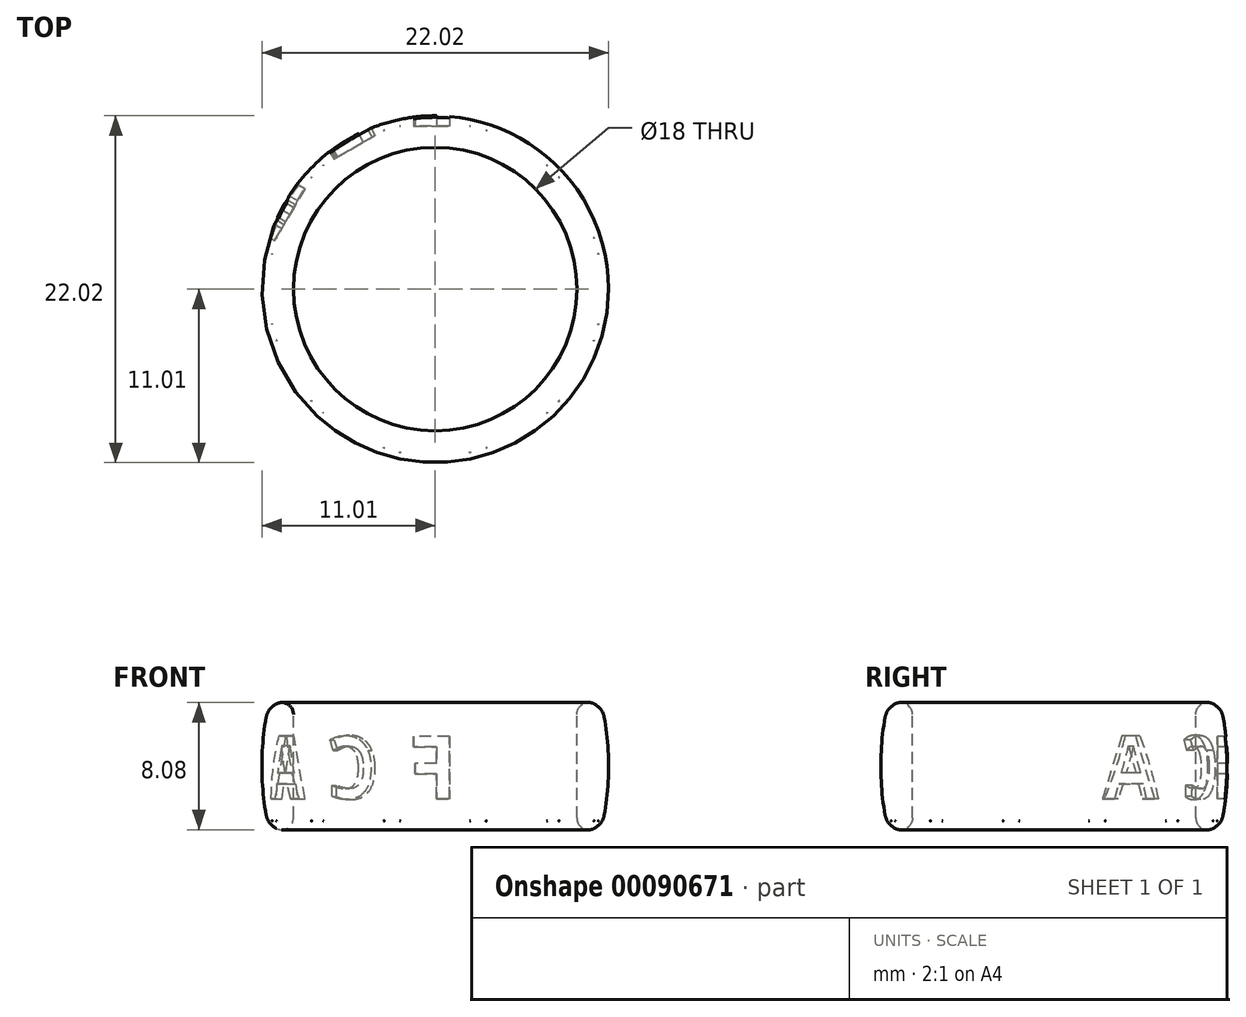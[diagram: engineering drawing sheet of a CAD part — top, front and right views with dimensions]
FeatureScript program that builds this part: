
annotation { "Feature Type Name" : "Feature", "Feature Type Description" : "" }
export const myFeature = defineFeature(function(context is Context, id is Id, definition is map)
    precondition{}
    {
        {
            var Q0;
            Q0=qCreatedBy(makeId("Top.planeOp"),FACE);
            var sketch = newSketch(context, id + "F0", { "sketchPlane" : qUnion([Q0])});
            skCircle(sketch, "E0", {"center": v(0, 0) * mm, "radius": 9 * mm});
            skSolve(sketch);
        }
        {
            var Q0;
            Q0 = qSketchRegion(id + "F0", true);
            extrude(context, id + "F1", {"entities" : qUnion([Q0]), "depth" : 5 * mm});
        }
        {
            var Q0;
            Q0=qCreatedBy(makeId("Front.planeOp"),FACE);
            var sketch = newSketch(context, id + "F2", { "sketchPlane" : qUnion([Q0])});
            skLineSegment(sketch, "E1", {"start": v(-9, 0) * mm, "end": v(-9, 8.18) * mm});
            skLineSegment(sketch, "E2", {"start": v(-9, 8.18) * mm, "end": v(-10.5, 8.18) * mm});
            skLineSegment(sketch, "E3", {"start": v(-9, 0) * mm, "end": v(-10.5, 0) * mm});
            skEllipticalArc(sketch, "E4", {});
            const initialGuessF2  = {"E4": [-0.009, 0.004088467297574947, 0, 1, 0.006151676925641073, 0.0020075208455440164, 0.8438243033653899, 2.2977683502244024]};
            skSetInitialGuess(sketch, initialGuessF2);
            skSolve(sketch);
        }
        {
            var Q0;
            Q0=makeQuery(id+"F2.imprint","IMPRINT",FACE,{"disambiguationData":[TD([[makeQuery(id+"F2.imprint","IMPRINT",EDGE,{"derivedFrom":sQuery(id+"F2.wireOp",EDGE,"E1")}),1.0]])]});
            var Q1;
            Q1=makeQuery(id+"F1.opExtrude","SWEPT_FACE",FACE,{"disambiguationData":[OSD([sQuery(id+"F0.wireOp",EDGE,"E0")])]});
            revolve(context, id + "F3", {"entities" : qUnion([Q0]), "axis" : qUnion([Q1]), "revolveType" : RevolveType.FULL});
        }
        {
            var Q0;
            Q0=makeQuery(id+"F3.opRevolve","SWEPT_EDGE",EDGE,{"disambiguationData":[OSD([sQuery(id+"F2.wireOp",EDGE,"E2"),sQuery(id+"F2.wireOp",EDGE,"E4")])]});
            var Q1;
            Q1=makeQuery(id+"F3.opRevolve","SWEPT_EDGE",EDGE,{"disambiguationData":[OSD([sQuery(id+"F2.wireOp",EDGE,"E3"),sQuery(id+"F2.wireOp",EDGE,"E4")])]});
            fillet(context, id + "F4", {"entities" : qUnion([Q0, Q1]), "radius" : 1.2 * mm, "tangentPropagation" : true, "allowEdgeOverflow" : false});
        }
        {
            var Q0;
            Q0=makeQuery(id+"F3.opRevolve","SWEPT_EDGE",EDGE,{"disambiguationData":[OSD([sQuery(id+"F2.wireOp",EDGE,"E1"),sQuery(id+"F2.wireOp",EDGE,"E3")])]});
            var Q1;
            Q1=makeQuery(id+"F3.opRevolve","SWEPT_EDGE",EDGE,{"disambiguationData":[OSD([sQuery(id+"F2.wireOp",EDGE,"E1"),sQuery(id+"F2.wireOp",EDGE,"E2")])]});
            fillet(context, id + "F5", {"entities" : qUnion([Q0, Q1]), "radius" : .75 * mm, "tangentPropagation" : true, "allowEdgeOverflow" : false});
        }
        {
            var Q0;
            Q0=makeQuery(id+"F1.opExtrude","SWEPT_BODY",BODY,{"disambiguationData":[OSD([sQuery(id+"F0.wireOp",EDGE,"E0")])]});
            deleteBodies(context, id + "F6", {"entities" : qUnion([Q0])});
        }
        {
            var Q0;
            Q0=qCreatedBy(makeId("Top.planeOp"),FACE);
            cPlane(context, id + "F7", {"entities" : qUnion([Q0]), "cplaneType" : CPlaneType.OFFSET, "offset" : 7 * mm, "width" : 150 * mm, "height" : 150 * mm});
        }
        {
            var Q0;
            Q0=qCreatedBy(id+"F7.planeOp",FACE);
            var sketch = newSketch(context, id + "F8", { "sketchPlane" : qUnion([Q0])});
            skLineSegment(sketch, "E5.bottom", {"start": v(-2.25, -9.36) * mm, "end": v(2.25, -9.36) * mm});
            skLineSegment(sketch, "E5.top", {"start": v(-2.25, -10.36) * mm, "end": v(2.25, -10.36) * mm});
            skLineSegment(sketch, "E5.left", {"start": v(-2.25, -9.36) * mm, "end": v(-2.25, -10.36) * mm});
            skLineSegment(sketch, "E5.right", {"start": v(2.25, -9.36) * mm, "end": v(2.25, -10.36) * mm});
            skLineSegment(sketch, "E6.1.0", {"start": v(2.73, -9.23) * mm, "end": v(6.63, -6.98) * mm});
            skLineSegment(sketch, "E6.1.1", {"start": v(6.63, -6.98) * mm, "end": v(7.13, -7.85) * mm});
            skLineSegment(sketch, "E6.1.2", {"start": v(3.23, -10.1) * mm, "end": v(7.13, -7.85) * mm});
            skLineSegment(sketch, "E6.1.3", {"start": v(2.73, -9.23) * mm, "end": v(3.23, -10.1) * mm});
            skLineSegment(sketch, "E6.2.0", {"start": v(6.98, -6.63) * mm, "end": v(9.23, -2.73) * mm});
            skLineSegment(sketch, "E6.2.1", {"start": v(9.23, -2.73) * mm, "end": v(10.1, -3.23) * mm});
            skLineSegment(sketch, "E6.2.2", {"start": v(7.85, -7.13) * mm, "end": v(10.1, -3.23) * mm});
            skLineSegment(sketch, "E6.2.3", {"start": v(6.98, -6.63) * mm, "end": v(7.85, -7.13) * mm});
            skLineSegment(sketch, "E6.3.0", {"start": v(9.36, -2.25) * mm, "end": v(9.36, 2.25) * mm});
            skLineSegment(sketch, "E6.3.1", {"start": v(9.36, 2.25) * mm, "end": v(10.36, 2.25) * mm});
            skLineSegment(sketch, "E6.3.2", {"start": v(10.36, -2.25) * mm, "end": v(10.36, 2.25) * mm});
            skLineSegment(sketch, "E6.3.3", {"start": v(9.36, -2.25) * mm, "end": v(10.36, -2.25) * mm});
            skLineSegment(sketch, "E6.4.0", {"start": v(9.23, 2.73) * mm, "end": v(6.98, 6.63) * mm});
            skLineSegment(sketch, "E6.4.1", {"start": v(6.98, 6.63) * mm, "end": v(7.85, 7.13) * mm});
            skLineSegment(sketch, "E6.4.2", {"start": v(10.1, 3.23) * mm, "end": v(7.85, 7.13) * mm});
            skLineSegment(sketch, "E6.4.3", {"start": v(9.23, 2.73) * mm, "end": v(10.1, 3.23) * mm});
            skLineSegment(sketch, "E6.5.0", {"start": v(6.63, 6.98) * mm, "end": v(2.73, 9.23) * mm});
            skLineSegment(sketch, "E6.5.1", {"start": v(2.73, 9.23) * mm, "end": v(3.23, 10.1) * mm});
            skLineSegment(sketch, "E6.5.2", {"start": v(7.13, 7.85) * mm, "end": v(3.23, 10.1) * mm});
            skLineSegment(sketch, "E6.5.3", {"start": v(6.63, 6.98) * mm, "end": v(7.13, 7.85) * mm});
            skLineSegment(sketch, "E6.6.0", {"start": v(2.25, 9.36) * mm, "end": v(-2.25, 9.36) * mm});
            skLineSegment(sketch, "E6.6.1", {"start": v(-2.25, 9.36) * mm, "end": v(-2.25, 10.36) * mm});
            skLineSegment(sketch, "E6.6.2", {"start": v(2.25, 10.36) * mm, "end": v(-2.25, 10.36) * mm});
            skLineSegment(sketch, "E6.6.3", {"start": v(2.25, 9.36) * mm, "end": v(2.25, 10.36) * mm});
            skLineSegment(sketch, "E6.7.0", {"start": v(-2.73, 9.23) * mm, "end": v(-6.63, 6.98) * mm});
            skLineSegment(sketch, "E6.7.1", {"start": v(-6.63, 6.98) * mm, "end": v(-7.13, 7.85) * mm});
            skLineSegment(sketch, "E6.7.2", {"start": v(-3.23, 10.1) * mm, "end": v(-7.13, 7.85) * mm});
            skLineSegment(sketch, "E6.7.3", {"start": v(-2.73, 9.23) * mm, "end": v(-3.23, 10.1) * mm});
            skLineSegment(sketch, "E6.8.0", {"start": v(-6.98, 6.63) * mm, "end": v(-9.23, 2.73) * mm});
            skLineSegment(sketch, "E6.8.1", {"start": v(-9.23, 2.73) * mm, "end": v(-10.1, 3.23) * mm});
            skLineSegment(sketch, "E6.8.2", {"start": v(-7.85, 7.13) * mm, "end": v(-10.1, 3.23) * mm});
            skLineSegment(sketch, "E6.8.3", {"start": v(-6.98, 6.63) * mm, "end": v(-7.85, 7.13) * mm});
            skLineSegment(sketch, "E6.9.0", {"start": v(-9.36, 2.25) * mm, "end": v(-9.36, -2.25) * mm});
            skLineSegment(sketch, "E6.9.1", {"start": v(-9.36, -2.25) * mm, "end": v(-10.36, -2.25) * mm});
            skLineSegment(sketch, "E6.9.2", {"start": v(-10.36, 2.25) * mm, "end": v(-10.36, -2.25) * mm});
            skLineSegment(sketch, "E6.9.3", {"start": v(-9.36, 2.25) * mm, "end": v(-10.36, 2.25) * mm});
            skLineSegment(sketch, "E6.10.0", {"start": v(-9.23, -2.73) * mm, "end": v(-6.98, -6.63) * mm});
            skLineSegment(sketch, "E6.10.1", {"start": v(-6.98, -6.63) * mm, "end": v(-7.85, -7.13) * mm});
            skLineSegment(sketch, "E6.10.2", {"start": v(-10.1, -3.23) * mm, "end": v(-7.85, -7.13) * mm});
            skLineSegment(sketch, "E6.10.3", {"start": v(-9.23, -2.73) * mm, "end": v(-10.1, -3.23) * mm});
            skLineSegment(sketch, "E6.11.0", {"start": v(-6.63, -6.98) * mm, "end": v(-2.73, -9.23) * mm});
            skLineSegment(sketch, "E6.11.1", {"start": v(-2.73, -9.23) * mm, "end": v(-3.23, -10.1) * mm});
            skLineSegment(sketch, "E6.11.2", {"start": v(-7.13, -7.85) * mm, "end": v(-3.23, -10.1) * mm});
            skLineSegment(sketch, "E6.11.3", {"start": v(-6.63, -6.98) * mm, "end": v(-7.13, -7.85) * mm});
            skPoint(sketch, "E6.center", {"position": v(0, 0) * mm});
            skSolve(sketch);
        }
        {
            var Q0;
            Q0 = qSketchRegion(id + "F8", true);
            extrude(context, id + "F9", {"entities" : qUnion([Q0]), "operationType" : NewBodyOperationType.ADD, "oppositeDirection" : true, "depth" : 6.4 * mm});
        }
        {
            var Q0;
            Q0=makeQuery(id+"F9.opExtrude","SWEPT_FACE",FACE,{"disambiguationData":[OSD([sQuery(id+"F8.wireOp",EDGE,"E6.6.2")])]});
            var sketch = newSketch(context, id + "F10", { "sketchPlane" : qUnion([Q0])});
            skText(sketch, "E7", { "text": "F", "fontName": "OpenSans-Bold.ttf"});
            const initialGuessF10  = {"E7": [-0.0014, 0.00202, 1, 0, 0.004]};
            skSetInitialGuess(sketch, initialGuessF10);
            skSolve(sketch);
        }
        {
            var Q0;
            Q0=makeQuery(id+"F10.imprint","IMPRINT",FACE,{"disambiguationData":[TD([[makeQuery(id+"F10.imprint","IMPRINT",EDGE,{"derivedFrom":sQuery(id+"F10.wireOp",EDGE,"E7.sketch_text.stroke-0")}),-1.0]])]});
            extrude(context, id + "F11", {"entities" : qUnion([Q0]), "operationType" : NewBodyOperationType.REMOVE, "depth" : 1 * mm});
        }
        {
            var Q0;
            Q0=makeQuery(id+"F9.opExtrude","SWEPT_FACE",FACE,{"disambiguationData":[OSD([sQuery(id+"F8.wireOp",EDGE,"E6.7.2")])]});
            var sketch = newSketch(context, id + "F12", { "sketchPlane" : qUnion([Q0])});
            skText(sketch, "E8", { "text": "C", "fontName": "OpenSans-Bold.ttf"});
            const initialGuessF12  = {"E8": [-0.0019, 0.00202, 1, 0, 0.004]};
            skSetInitialGuess(sketch, initialGuessF12);
            skSolve(sketch);
        }
        {
            var Q0;
            Q0 = qSketchRegion(id + "F12", true);
            extrude(context, id + "F13", {"entities" : qUnion([Q0]), "operationType" : NewBodyOperationType.REMOVE, "depth" : 1 * mm});
        }
        {
            var Q0;
            Q0=makeQuery(id+"F9.opExtrude","SWEPT_FACE",FACE,{"disambiguationData":[OSD([sQuery(id+"F8.wireOp",EDGE,"E6.8.2")])]});
            var sketch = newSketch(context, id + "F14", { "sketchPlane" : qUnion([Q0])});
            skText(sketch, "E9", { "text": "A", "fontName": "OpenSans-Bold.ttf"});
            const initialGuessF14  = {"E9": [-0.0014, 0.00202, 1, 0, 0.004]};
            skSetInitialGuess(sketch, initialGuessF14);
            skSolve(sketch);
        }
        {
            var Q0;
            Q0 = qSketchRegion(id + "F14", true);
            extrude(context, id + "F15", {"entities" : qUnion([Q0]), "operationType" : NewBodyOperationType.REMOVE, "depth" : 1 * mm});
        }
    });
